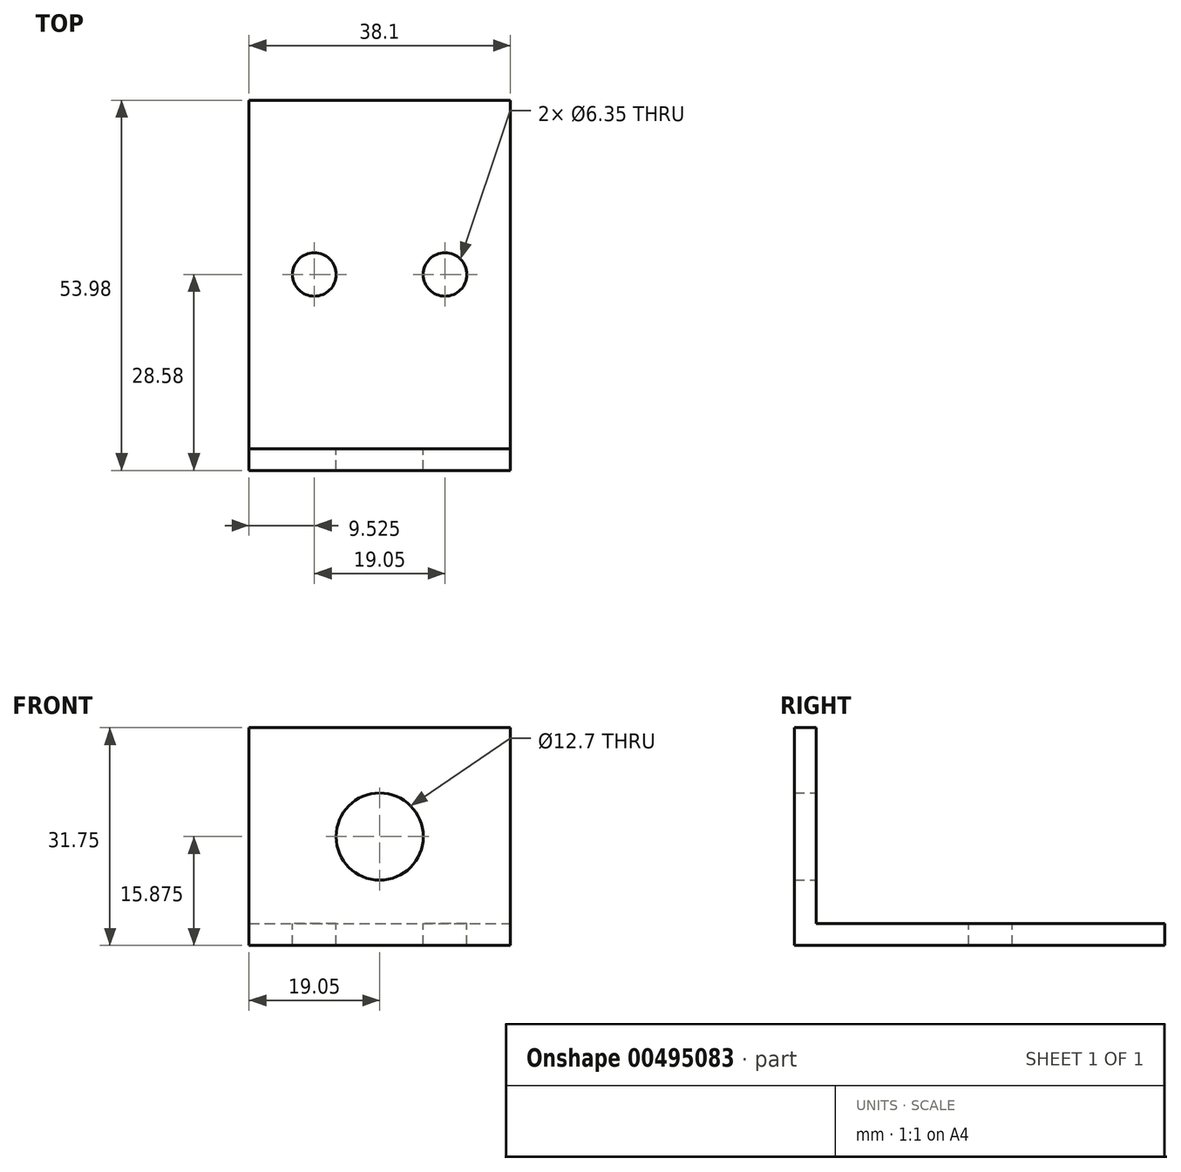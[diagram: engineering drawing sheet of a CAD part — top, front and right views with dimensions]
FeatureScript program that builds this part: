
annotation { "Feature Type Name" : "Feature", "Feature Type Description" : "" }
export const myFeature = defineFeature(function(context is Context, id is Id, definition is map)
    precondition{}
    {
        {
            var Q0;
            Q0=qCreatedBy(makeId("Front.planeOp"),FACE);
            var sketch = newSketch(context, id + "F0", { "sketchPlane" : qUnion([Q0])});
            skLineSegment(sketch, "E0.bottom", {"start": v(0, 0) * mm, "end": v(38.1, 0) * mm});
            skLineSegment(sketch, "E0.top", {"start": v(0, 31.75) * mm, "end": v(38.1, 31.75) * mm});
            skLineSegment(sketch, "E0.left", {"start": v(0, 0) * mm, "end": v(0, 31.75) * mm});
            skLineSegment(sketch, "E0.right", {"start": v(38.1, 0) * mm, "end": v(38.1, 31.75) * mm});
            skCircle(sketch, "E1", {"center": v(19.05, 15.88) * mm, "radius": 6.35 * mm});
            skSolve(sketch);
        }
        {
            var Q0;
            Q0=makeQuery(id+"F0.imprint","IMPRINT",FACE,{"disambiguationData":[TD([[makeQuery(id+"F0.imprint","IMPRINT",EDGE,{"derivedFrom":sQuery(id+"F0.wireOp",EDGE,"E0.bottom")}),1.0]])]});
            extrude(context, id + "F1", {"entities" : qUnion([Q0]), "depth" : 3.17 * mm});
        }
        {
            var Q0;
            Q0=makeQuery(id+"F1.opExtrude","CAP_FACE",FACE,{"disambiguationData":[OSD([sQuery(id+"F0.wireOp",EDGE,"E0.bottom"),sQuery(id+"F0.wireOp",EDGE,"E0.top"),sQuery(id+"F0.wireOp",EDGE,"E0.left"),sQuery(id+"F0.wireOp",EDGE,"E0.right"),sQuery(id+"F0.wireOp",EDGE,"E1")])],"isStart":true});
            var sketch = newSketch(context, id + "F2", { "sketchPlane" : qUnion([Q0])});
            skLineSegment(sketch, "E2.bottom", {"start": v(0, 0) * mm, "end": v(-38.1, 0) * mm});
            skLineSegment(sketch, "E2.top", {"start": v(0, 3.17) * mm, "end": v(-38.1, 3.17) * mm});
            skLineSegment(sketch, "E2.left", {"start": v(0, 0) * mm, "end": v(0, 3.17) * mm});
            skLineSegment(sketch, "E2.right", {"start": v(-38.1, 0) * mm, "end": v(-38.1, 3.17) * mm});
            skSolve(sketch);
        }
        {
            var Q0;
            Q0=makeQuery(id+"F2.imprint","IMPRINT",FACE,{"disambiguationData":[TD([[makeQuery(id+"F2.imprint","IMPRINT",EDGE,{"derivedFrom":sQuery(id+"F2.wireOp",EDGE,"E2.bottom")}),-1.0]])]});
            extrude(context, id + "F3", {"entities" : qUnion([Q0]), "operationType" : NewBodyOperationType.ADD, "depth" : 50.8 * mm});
        }
        {
            var Q0;
            Q0=makeQuery(id+"F3.opExtrude","SWEPT_FACE",FACE,{"disambiguationData":[OSD([sQuery(id+"F2.wireOp",EDGE,"E2.top")])]});
            var sketch = newSketch(context, id + "F4", { "sketchPlane" : qUnion([Q0])});
            skCircle(sketch, "E3", {"center": v(9.53, 25.4) * mm, "radius": 3.18 * mm});
            skCircle(sketch, "E4", {"center": v(28.58, 25.4) * mm, "radius": 3.18 * mm});
            skSolve(sketch);
        }
        {
            var Q0;
            Q0=makeQuery(id+"F4.imprint","IMPRINT",FACE,{"disambiguationData":[TD([[makeQuery(id+"F4.imprint","IMPRINT",EDGE,{"derivedFrom":sQuery(id+"F4.wireOp",EDGE,"E4")}),1.0]])]});
            var Q1;
            Q1=makeQuery(id+"F4.imprint","IMPRINT",FACE,{"disambiguationData":[TD([[makeQuery(id+"F4.imprint","IMPRINT",EDGE,{"derivedFrom":sQuery(id+"F4.wireOp",EDGE,"E3")}),1.0]])]});
            extrude(context, id + "F5", {"entities" : qUnion([Q0, Q1]), "operationType" : NewBodyOperationType.REMOVE, "endBound" : BoundingType.THROUGH_ALL, "oppositeDirection" : true, "depth" : 25.4 * mm});
        }
    });
